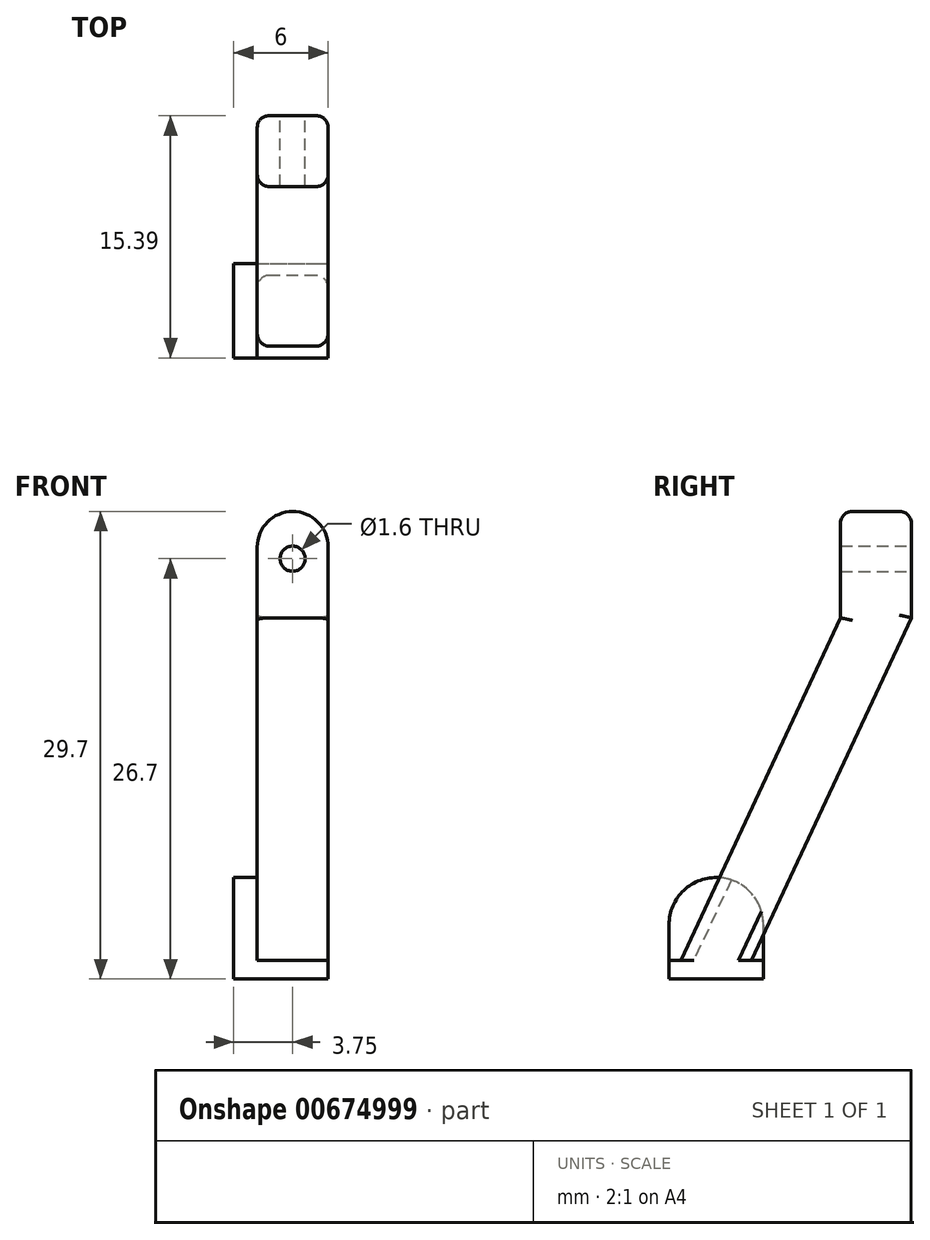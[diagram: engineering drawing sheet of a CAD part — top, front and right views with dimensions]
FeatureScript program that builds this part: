
annotation { "Feature Type Name" : "Feature", "Feature Type Description" : "" }
export const myFeature = defineFeature(function(context is Context, id is Id, definition is map)
    precondition{}
    {
        {
            assignVariable(context, id + "F0", {"name" : "Faktor", "anyValue" : 1.5});
        }
        {
            var Q0;
            Q0=qCreatedBy(makeId("Top.planeOp"),FACE);
            var sketch = newSketch(context, id + "F1", { "sketchPlane" : qUnion([Q0])});
            skLineSegment(sketch, "E0.bottom", {"start": v(0, 0) * mm, "end": v(6, 0) * mm});
            skLineSegment(sketch, "E0.top", {"start": v(0, 6) * mm, "end": v(6, 6) * mm});
            skLineSegment(sketch, "E0.left", {"start": v(0, 0) * mm, "end": v(0, 6) * mm});
            skLineSegment(sketch, "E0.right", {"start": v(6, 0) * mm, "end": v(6, 6) * mm});
            skSolve(sketch);
        }
        {
            var Q0;
            Q0=qSketchRegion(id+"F1",true);
            extrude(context, id + "F2", {"entities" : qUnion([Q0]), "depth" : getVariable(context, 'Faktor') * 0.8 * mm, "offsetDistance" : 25 * mm});
        }
        {
            var Q0;
            Q0=qCreatedBy(makeId("Right.planeOp"),FACE);
            cPlane(context, id + "F3", {"entities" : qUnion([Q0]), "cplaneType" : CPlaneType.OFFSET, "offset" : getVariable(context, 'Faktor') * 2.5 * mm, "width" : 150 * mm, "height" : 150 * mm});
        }
        {
            var Q0;
            Q0=qCreatedBy(id+"F3.planeOp",FACE);
            var sketch = newSketch(context, id + "F4", { "sketchPlane" : qUnion([Q0])});
            skLineSegment(sketch, "E1", {"start": v(5.25, 1.2) * mm, "end": v(15.4, 22.95) * mm});
            skLineSegment(sketch, "E2", {"start": v(10.9, 22.95) * mm, "end": v(0.75, 1.2) * mm});
            skLineSegment(sketch, "E3", {"start": v(0.75, 1.2) * mm, "end": v(5.25, 1.2) * mm});
            skLineSegment(sketch, "E4", {"start": v(10.9, 22.95) * mm, "end": v(10.9, 29.7) * mm});
            skLineSegment(sketch, "E5", {"start": v(10.9, 29.7) * mm, "end": v(15.4, 29.7) * mm});
            skLineSegment(sketch, "E6", {"start": v(15.4, 29.7) * mm, "end": v(15.4, 22.95) * mm});
            skLineSegment(sketch, "E7", {"start": v(10.9, 22.95) * mm, "end": v(18.63, 22.95) * mm, "construction": true});
            skSolve(sketch);
        }
        {
            var Q0;
            Q0=qSketchRegion(id+"F4",true);
            extrude(context, id + "F5", {"entities" : qUnion([Q0]), "operationType" : NewBodyOperationType.ADD, "endBound" : BoundingType.SYMMETRIC, "depth" : getVariable(context, 'Faktor') * 3 * mm, "offsetDistance" : 25 * mm});
        }
        {
            var Q0;
            Q0=makeQuery(id+"F5.opExtrude","SWEPT_FACE",FACE,{"disambiguationData":[OSD([sQuery(id+"F4.wireOp",EDGE,"E6")])]});
            var sketch = newSketch(context, id + "F6", { "sketchPlane" : qUnion([Q0])});
            skCircle(sketch, "E8", {"center": v(-3.75, 26.7) * mm, "radius": 0.8 * mm});
            skSolve(sketch);
        }
        {
            var Q0;
            Q0=qSketchRegion(id+"F6",true);
            extrude(context, id + "F7", {"entities" : qUnion([Q0]), "operationType" : NewBodyOperationType.REMOVE, "endBound" : BoundingType.THROUGH_ALL, "oppositeDirection" : true, "depth" : 25 * mm, "offsetDistance" : 25 * mm});
        }
        {
            var Q0;
            Q0=makeQuery(id+"F5.opExtrude","CAP_EDGE",EDGE,{"disambiguationData":[OSD([sQuery(id+"F4.wireOp",EDGE,"E5")])],"isStart":true});
            var Q1;
            Q1=makeQuery(id+"F5.opExtrude","CAP_EDGE",EDGE,{"disambiguationData":[OSD([sQuery(id+"F4.wireOp",EDGE,"E5")])],"isStart":false});
            fillet(context, id + "F8", {"entities" : qUnion([Q0, Q1]), "radius" : getVariable(context, 'Faktor') * 1.5 * mm, "tangentPropagation" : true, "allowEdgeOverflow" : false});
        }
        {
            var Q0;
            Q0=makeQuery(id+"F5.opExtrude","CAP_EDGE",EDGE,{"disambiguationData":[OSD([sQuery(id+"F4.wireOp",EDGE,"E1")])],"isStart":true});
            var Q1;
            Q1=makeQuery(id+"F5.opExtrude","CAP_EDGE",EDGE,{"disambiguationData":[OSD([sQuery(id+"F4.wireOp",EDGE,"E6")])],"isStart":true});
            var Q2;
            Q2=makeQuery(id+"F8.opFillet","BLEND_EDGE",EDGE,{"blendedFrom":[makeQuery(id+"F5.opExtrude","CAP_EDGE",EDGE,{"disambiguationData":[OSD([sQuery(id+"F4.wireOp",EDGE,"E5")])],"isStart":false}),makeQuery(id+"F5.opExtrude","SWEPT_FACE",FACE,{"disambiguationData":[OSD([sQuery(id+"F4.wireOp",EDGE,"E6")])]})],"blendedInto":[makeQuery(id+"F5.opExtrude","SWEPT_FACE",FACE,{"disambiguationData":[OSD([sQuery(id+"F4.wireOp",EDGE,"E6")])]})]});
            var Q3;
            Q3=makeQuery(id+"F5.opExtrude","CAP_EDGE",EDGE,{"disambiguationData":[OSD([sQuery(id+"F4.wireOp",EDGE,"E1")])],"isStart":false});
            var Q4;
            Q4=makeQuery(id+"F5.opExtrude","CAP_EDGE",EDGE,{"disambiguationData":[OSD([sQuery(id+"F4.wireOp",EDGE,"E2")])],"isStart":true});
            var Q5;
            Q5=makeQuery(id+"F5.opExtrude","CAP_EDGE",EDGE,{"disambiguationData":[OSD([sQuery(id+"F4.wireOp",EDGE,"E4")])],"isStart":true});
            var Q6;
            Q6=makeQuery(id+"F5.opExtrude","CAP_EDGE",EDGE,{"disambiguationData":[OSD([sQuery(id+"F4.wireOp",EDGE,"E2")])],"isStart":false});
            fillet(context, id + "F9", {"entities" : qUnion([Q0, Q1, Q2, Q3, Q4, Q5, Q6]), "radius" : getVariable(context, 'Faktor') * 0.5 * mm, "tangentPropagation" : true, "allowEdgeOverflow" : false});
        }
        {
            var Q0;
            Q0=makeQuery(id+"F2.opExtrude","SWEPT_FACE",FACE,{"disambiguationData":[OSD([sQuery(id+"F1.wireOp",EDGE,"E0.left")])]});
            var sketch = newSketch(context, id + "F10", { "sketchPlane" : qUnion([Q0])});
            skLineSegment(sketch, "E9.bottom", {"start": v(-6, 1.2) * mm, "end": v(0, 1.2) * mm});
            skLineSegment(sketch, "E9.top", {"start": v(-3, 6.45) * mm, "end": v(-3, 6.45) * mm});
            skLineSegment(sketch, "E9.left", {"start": v(-6, 1.2) * mm, "end": v(-6, 3.45) * mm});
            skLineSegment(sketch, "E9.right", {"start": v(0, 1.2) * mm, "end": v(0, 3.45) * mm});
            skPoint(sketch, "E10.visualSharp", {"position": v(-6, 6.45) * mm});
            skArc(sketch, "E10.filletArc", {"start": v(-3, 6.45) * mm, "mid": v(-5.12, 5.57) * mm, "end": v(-6, 3.45) * mm});
            skPoint(sketch, "E11.visualSharp", {"position": v(0, 6.45) * mm});
            skArc(sketch, "E11.filletArc", {"start": v(0, 3.45) * mm, "mid": v(-0.88, 5.57) * mm, "end": v(-3, 6.45) * mm});
            skSolve(sketch);
        }
        {
            var Q0;
            Q0=qSketchRegion(id+"F10",true);
            extrude(context, id + "F11", {"entities" : qUnion([Q0]), "operationType" : NewBodyOperationType.ADD, "oppositeDirection" : true, "depth" : getVariable(context, 'Faktor') * 1 * mm, "offsetDistance" : 25 * mm});
        }
    });
